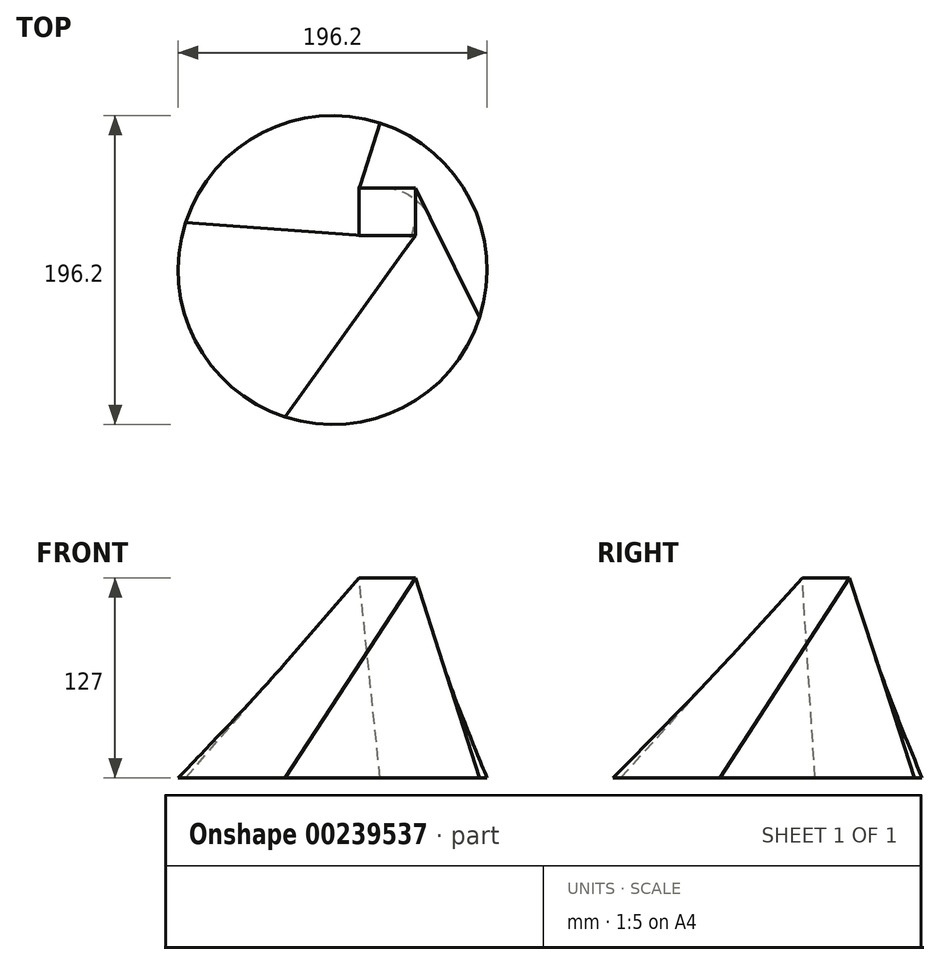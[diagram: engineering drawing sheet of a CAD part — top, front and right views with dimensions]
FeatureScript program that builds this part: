
annotation { "Feature Type Name" : "Feature", "Feature Type Description" : "" }
export const myFeature = defineFeature(function(context is Context, id is Id, definition is map)
    precondition{}
    {
        {
            var Q0;
            Q0=qCreatedBy(makeId("Top.planeOp"),FACE);
            cPlane(context, id + "F0", {"entities" : qUnion([Q0]), "cplaneType" : CPlaneType.OFFSET, "offset" : 127 * mm, "width" : 152.4 * mm, "height" : 152.4 * mm});
        }
        {
            var Q0;
            Q0=qCreatedBy(makeId("Top.planeOp"),FACE);
            var sketch = newSketch(context, id + "F1", { "sketchPlane" : qUnion([Q0])});
            skCircle(sketch, "E0", {"center": v(0, 0) * mm, "radius": 98.1 * mm});
            skSolve(sketch);
        }
        {
            var Q0;
            Q0=qCreatedBy(id+"F0.planeOp",FACE);
            var sketch = newSketch(context, id + "F2", { "sketchPlane" : qUnion([Q0])});
            skLineSegment(sketch, "E1.bottom", {"start": v(16.84, 52.1) * mm, "end": v(52.5, 52.1) * mm});
            skLineSegment(sketch, "E1.top", {"start": v(16.84, 22.05) * mm, "end": v(52.5, 22.05) * mm});
            skLineSegment(sketch, "E1.left", {"start": v(16.84, 52.1) * mm, "end": v(16.84, 22.05) * mm});
            skLineSegment(sketch, "E1.right", {"start": v(52.5, 52.1) * mm, "end": v(52.5, 22.05) * mm});
            skSolve(sketch);
        }
        {
            var Q0;
            Q0 = qSketchRegion(id + "F1", true);
            var Q1;
            Q1 = qSketchRegion(id + "F2", true);
            loft(context, id + "F3", {"sheetProfilesArray" : [{ "sheetProfileEntities" : qUnion([Q0]) }, { "sheetProfileEntities" : qUnion([Q1]) }]});
        }
    });
